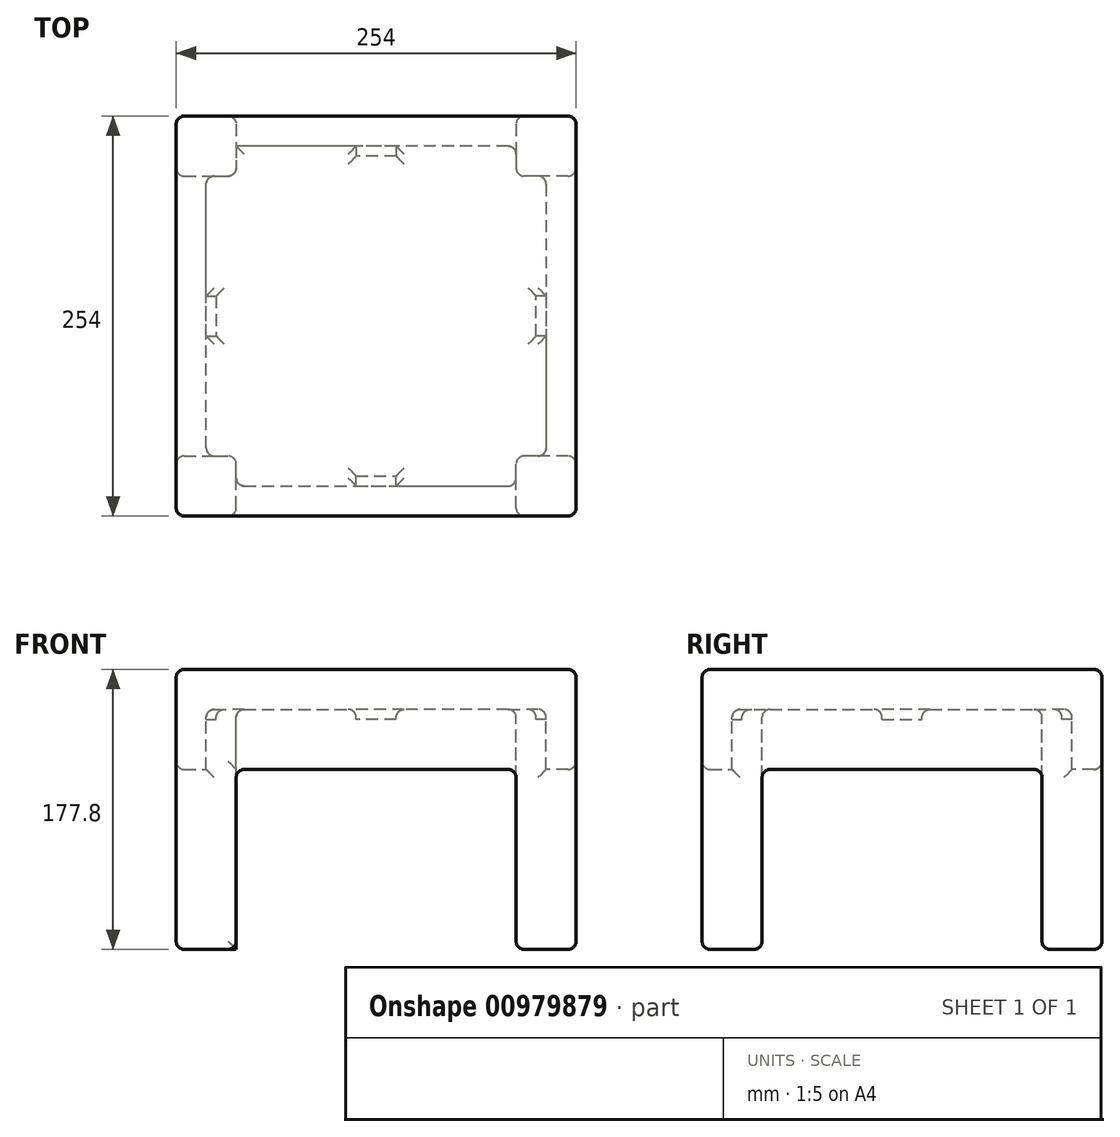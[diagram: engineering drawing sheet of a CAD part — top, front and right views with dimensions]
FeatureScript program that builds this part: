
annotation { "Feature Type Name" : "Feature", "Feature Type Description" : "" }
export const myFeature = defineFeature(function(context is Context, id is Id, definition is map)
    precondition{}
    {
        {
            var Q0;
            Q0=qCreatedBy(makeId("Top.planeOp"),FACE);
            var sketch = newSketch(context, id + "F0", { "sketchPlane" : qUnion([Q0])});
            skLineSegment(sketch, "E0", {"start": v(0, -127) * mm, "end": v(0, 127) * mm, "construction": true});
            skLineSegment(sketch, "E1", {"start": v(-127, 0) * mm, "end": v(127, 0) * mm, "construction": true});
            skLineSegment(sketch, "E2.bottom", {"start": v(-127, 127) * mm, "end": v(127, 127) * mm});
            skLineSegment(sketch, "E2.top", {"start": v(-127, -127) * mm, "end": v(127, -127) * mm});
            skLineSegment(sketch, "E2.left", {"start": v(-127, 127) * mm, "end": v(-127, -127) * mm});
            skLineSegment(sketch, "E2.right", {"start": v(127, 127) * mm, "end": v(127, -127) * mm});
            skSolve(sketch);
        }
        {
            var Q0;
            Q0 = qSketchRegion(id + "F0", true);
            extrude(context, id + "F1", {"entities" : qUnion([Q0]), "depth" : 25.4 * mm, "offsetDistance" : 25.4 * mm});
        }
        {
            var Q0;
            Q0=makeQuery(id+"F1.opExtrude","CAP_FACE",FACE,{"disambiguationData":[OSD([sQuery(id+"F0.wireOp",EDGE,"E2.bottom"),sQuery(id+"F0.wireOp",EDGE,"E2.top"),sQuery(id+"F0.wireOp",EDGE,"E2.left"),sQuery(id+"F0.wireOp",EDGE,"E2.right")])],"isStart":true});
            var sketch = newSketch(context, id + "F2", { "sketchPlane" : qUnion([Q0])});
            skLineSegment(sketch, "E3", {"start": v(0, 127) * mm, "end": v(0, -127) * mm, "construction": true});
            skLineSegment(sketch, "E4", {"start": v(-127, 0) * mm, "end": v(127, 0) * mm, "construction": true});
            skLineSegment(sketch, "E5.bottom", {"start": v(-127, 127) * mm, "end": v(-88.9, 127) * mm});
            skLineSegment(sketch, "E5.top", {"start": v(-127, 88.9) * mm, "end": v(-88.9, 88.9) * mm});
            skLineSegment(sketch, "E5.left", {"start": v(-127, 127) * mm, "end": v(-127, 88.9) * mm});
            skLineSegment(sketch, "E5.right", {"start": v(-88.9, 127) * mm, "end": v(-88.9, 88.9) * mm});
            skLineSegment(sketch, "E6.bottom", {"start": v(127, 127) * mm, "end": v(88.9, 127) * mm});
            skLineSegment(sketch, "E6.top", {"start": v(127, 88.9) * mm, "end": v(88.9, 88.9) * mm});
            skLineSegment(sketch, "E6.left", {"start": v(127, 127) * mm, "end": v(127, 88.9) * mm});
            skLineSegment(sketch, "E6.right", {"start": v(88.9, 127) * mm, "end": v(88.9, 88.9) * mm});
            skLineSegment(sketch, "E7.bottom", {"start": v(127, -127) * mm, "end": v(88.9, -127) * mm});
            skLineSegment(sketch, "E7.top", {"start": v(127, -88.9) * mm, "end": v(88.9, -88.9) * mm});
            skLineSegment(sketch, "E7.left", {"start": v(127, -127) * mm, "end": v(127, -88.9) * mm});
            skLineSegment(sketch, "E7.right", {"start": v(88.9, -127) * mm, "end": v(88.9, -88.9) * mm});
            skLineSegment(sketch, "E8.bottom", {"start": v(-127, -127) * mm, "end": v(-88.9, -127) * mm});
            skLineSegment(sketch, "E8.top", {"start": v(-127, -88.9) * mm, "end": v(-88.9, -88.9) * mm});
            skLineSegment(sketch, "E8.left", {"start": v(-127, -127) * mm, "end": v(-127, -88.9) * mm});
            skLineSegment(sketch, "E8.right", {"start": v(-88.9, -127) * mm, "end": v(-88.9, -88.9) * mm});
            skSolve(sketch);
        }
        {
            var Q0;
            Q0 = qSketchRegion(id + "F2", true);
            extrude(context, id + "F3", {"entities" : qUnion([Q0]), "operationType" : NewBodyOperationType.ADD, "depth" : 152.4 * mm, "offsetDistance" : 25.4 * mm});
        }
        {
            var Q0;
            Q0=makeQuery(id+"F1.opExtrude","CAP_FACE",FACE,{"disambiguationData":[OSD([sQuery(id+"F0.wireOp",EDGE,"E2.bottom"),sQuery(id+"F0.wireOp",EDGE,"E2.top"),sQuery(id+"F0.wireOp",EDGE,"E2.left"),sQuery(id+"F0.wireOp",EDGE,"E2.right")])],"isStart":true});
            var sketch = newSketch(context, id + "F4", { "sketchPlane" : qUnion([Q0])});
            skLineSegment(sketch, "E9", {"start": v(0, 127) * mm, "end": v(0, -127) * mm, "construction": true});
            skLineSegment(sketch, "E10", {"start": v(-127, 0) * mm, "end": v(127, 0) * mm, "construction": true});
            skLineSegment(sketch, "E11.bottom", {"start": v(-88.9, 127) * mm, "end": v(88.9, 127) * mm});
            skLineSegment(sketch, "E11.top", {"start": v(-88.9, 107.95) * mm, "end": v(88.9, 107.95) * mm});
            skLineSegment(sketch, "E11.left", {"start": v(-88.9, 127) * mm, "end": v(-88.9, 107.95) * mm});
            skLineSegment(sketch, "E11.right", {"start": v(88.9, 127) * mm, "end": v(88.9, 107.95) * mm});
            skLineSegment(sketch, "E12.bottom", {"start": v(-127, 88.9) * mm, "end": v(-107.95, 88.9) * mm});
            skLineSegment(sketch, "E12.top", {"start": v(-127, -88.9) * mm, "end": v(-107.95, -88.9) * mm});
            skLineSegment(sketch, "E12.left", {"start": v(-127, 88.9) * mm, "end": v(-127, -88.9) * mm});
            skLineSegment(sketch, "E12.right", {"start": v(-107.95, 88.9) * mm, "end": v(-107.95, -88.9) * mm});
            skLineSegment(sketch, "E13.bottom", {"start": v(127, -88.9) * mm, "end": v(107.95, -88.9) * mm});
            skLineSegment(sketch, "E13.top", {"start": v(127, 88.9) * mm, "end": v(107.95, 88.9) * mm});
            skLineSegment(sketch, "E13.left", {"start": v(127, -88.9) * mm, "end": v(127, 88.9) * mm});
            skLineSegment(sketch, "E13.right", {"start": v(107.95, -88.9) * mm, "end": v(107.95, 88.9) * mm});
            skLineSegment(sketch, "E14.bottom", {"start": v(88.9, -127) * mm, "end": v(-88.9, -127) * mm});
            skLineSegment(sketch, "E14.top", {"start": v(88.9, -107.95) * mm, "end": v(-88.9, -107.95) * mm});
            skLineSegment(sketch, "E14.left", {"start": v(88.9, -127) * mm, "end": v(88.9, -107.95) * mm});
            skLineSegment(sketch, "E14.right", {"start": v(-88.9, -127) * mm, "end": v(-88.9, -107.95) * mm});
            skSolve(sketch);
        }
        {
            var Q0;
            Q0 = qSketchRegion(id + "F4", true);
            extrude(context, id + "F5", {"entities" : qUnion([Q0]), "operationType" : NewBodyOperationType.ADD, "depth" : 38.1 * mm, "offsetDistance" : 25.4 * mm});
        }
        {
            var Q0;
            Q0=makeQuery(id+"F1.opExtrude","CAP_FACE",FACE,{"disambiguationData":[OSD([sQuery(id+"F0.wireOp",EDGE,"E2.bottom"),sQuery(id+"F0.wireOp",EDGE,"E2.top"),sQuery(id+"F0.wireOp",EDGE,"E2.left"),sQuery(id+"F0.wireOp",EDGE,"E2.right")])],"isStart":true});
            var sketch = newSketch(context, id + "F6", { "sketchPlane" : qUnion([Q0])});
            skLineSegment(sketch, "E15", {"start": v(0, 107.95) * mm, "end": v(0, -107.95) * mm, "construction": true});
            skLineSegment(sketch, "E16", {"start": v(-107.95, 0) * mm, "end": v(107.95, 0) * mm, "construction": true});
            skLineSegment(sketch, "E17.bottom", {"start": v(-107.95, -12.7) * mm, "end": v(-101.6, -12.7) * mm});
            skLineSegment(sketch, "E17.top", {"start": v(-107.95, 12.7) * mm, "end": v(-101.6, 12.7) * mm});
            skLineSegment(sketch, "E17.left", {"start": v(-107.95, -12.7) * mm, "end": v(-107.95, 12.7) * mm});
            skLineSegment(sketch, "E17.right", {"start": v(-101.6, -12.7) * mm, "end": v(-101.6, 12.7) * mm});
            skLineSegment(sketch, "E18.bottom", {"start": v(-12.7, 107.95) * mm, "end": v(12.7, 107.95) * mm});
            skLineSegment(sketch, "E18.top", {"start": v(-12.7, 101.6) * mm, "end": v(12.7, 101.6) * mm});
            skLineSegment(sketch, "E18.left", {"start": v(-12.7, 107.95) * mm, "end": v(-12.7, 101.6) * mm});
            skLineSegment(sketch, "E18.right", {"start": v(12.7, 107.95) * mm, "end": v(12.7, 101.6) * mm});
            skLineSegment(sketch, "E19.bottom", {"start": v(107.95, 12.7) * mm, "end": v(101.6, 12.7) * mm});
            skLineSegment(sketch, "E19.top", {"start": v(107.95, -12.7) * mm, "end": v(101.6, -12.7) * mm});
            skLineSegment(sketch, "E19.left", {"start": v(107.95, 12.7) * mm, "end": v(107.95, -12.7) * mm});
            skLineSegment(sketch, "E19.right", {"start": v(101.6, 12.7) * mm, "end": v(101.6, -12.7) * mm});
            skLineSegment(sketch, "E20.bottom", {"start": v(12.7, -107.95) * mm, "end": v(-12.7, -107.95) * mm});
            skLineSegment(sketch, "E20.top", {"start": v(12.7, -101.6) * mm, "end": v(-12.7, -101.6) * mm});
            skLineSegment(sketch, "E20.left", {"start": v(12.7, -107.95) * mm, "end": v(12.7, -101.6) * mm});
            skLineSegment(sketch, "E20.right", {"start": v(-12.7, -107.95) * mm, "end": v(-12.7, -101.6) * mm});
            skSolve(sketch);
        }
        {
            var Q0;
            Q0 = qSketchRegion(id + "F6", true);
            extrude(context, id + "F7", {"entities" : qUnion([Q0]), "operationType" : NewBodyOperationType.ADD, "depth" : 6.35 * mm, "offsetDistance" : 25.4 * mm});
        }
        {
            var Q0;
            Q0=makeQuery(id+"F5.boolean.opBoolean","MERGE",FACE,{"derivedFrom":[makeQuery(id+"F3.boolean.opBoolean","MERGE",FACE,{"derivedFrom":[makeQuery(id+"F1.opExtrude","SWEPT_FACE",FACE,{"disambiguationData":[OSD([sQuery(id+"F0.wireOp",EDGE,"E2.top")])]}),makeQuery(id+"F3.opExtrude","SWEPT_FACE",FACE,{"disambiguationData":[OSD([sQuery(id+"F2.wireOp",EDGE,"E5.bottom")])]}),makeQuery(id+"F3.opExtrude","SWEPT_FACE",FACE,{"disambiguationData":[OSD([sQuery(id+"F2.wireOp",EDGE,"E6.bottom")])]})]}),makeQuery(id+"F5.opExtrude","SWEPT_FACE",FACE,{"disambiguationData":[OSD([sQuery(id+"F4.wireOp",EDGE,"E11.bottom")])]})]});
            var Q1;
            Q1=makeQuery(id+"F5.boolean.opBoolean","MERGE",FACE,{"derivedFrom":[makeQuery(id+"F3.boolean.opBoolean","MERGE",FACE,{"derivedFrom":[makeQuery(id+"F1.opExtrude","SWEPT_FACE",FACE,{"disambiguationData":[OSD([sQuery(id+"F0.wireOp",EDGE,"E2.right")])]}),makeQuery(id+"F3.opExtrude","SWEPT_FACE",FACE,{"disambiguationData":[OSD([sQuery(id+"F2.wireOp",EDGE,"E6.left")])]}),makeQuery(id+"F3.opExtrude","SWEPT_FACE",FACE,{"disambiguationData":[OSD([sQuery(id+"F2.wireOp",EDGE,"E7.left")])]})]}),makeQuery(id+"F5.opExtrude","SWEPT_FACE",FACE,{"disambiguationData":[OSD([sQuery(id+"F4.wireOp",EDGE,"E13.left")])]})]});
            var Q2;
            Q2=makeQuery(id+"F5.boolean.opBoolean","MERGE",FACE,{"derivedFrom":[makeQuery(id+"F3.boolean.opBoolean","MERGE",FACE,{"derivedFrom":[makeQuery(id+"F1.opExtrude","SWEPT_FACE",FACE,{"disambiguationData":[OSD([sQuery(id+"F0.wireOp",EDGE,"E2.bottom")])]}),makeQuery(id+"F3.opExtrude","SWEPT_FACE",FACE,{"disambiguationData":[OSD([sQuery(id+"F2.wireOp",EDGE,"E7.bottom")])]}),makeQuery(id+"F3.opExtrude","SWEPT_FACE",FACE,{"disambiguationData":[OSD([sQuery(id+"F2.wireOp",EDGE,"E8.bottom")])]})]}),makeQuery(id+"F5.opExtrude","SWEPT_FACE",FACE,{"disambiguationData":[OSD([sQuery(id+"F4.wireOp",EDGE,"E14.bottom")])]})]});
            var Q3;
            Q3=makeQuery(id+"F5.boolean.opBoolean","MERGE",FACE,{"derivedFrom":[makeQuery(id+"F3.boolean.opBoolean","MERGE",FACE,{"derivedFrom":[makeQuery(id+"F1.opExtrude","SWEPT_FACE",FACE,{"disambiguationData":[OSD([sQuery(id+"F0.wireOp",EDGE,"E2.left")])]}),makeQuery(id+"F3.opExtrude","SWEPT_FACE",FACE,{"disambiguationData":[OSD([sQuery(id+"F2.wireOp",EDGE,"E5.left")])]}),makeQuery(id+"F3.opExtrude","SWEPT_FACE",FACE,{"disambiguationData":[OSD([sQuery(id+"F2.wireOp",EDGE,"E8.left")])]})]}),makeQuery(id+"F5.opExtrude","SWEPT_FACE",FACE,{"disambiguationData":[OSD([sQuery(id+"F4.wireOp",EDGE,"E12.left")])]})]});
            var Q4;
            Q4=makeQuery(id+"F3.opExtrude","SWEPT_FACE",FACE,{"disambiguationData":[OSD([sQuery(id+"F2.wireOp",EDGE,"E7.right")])]});
            var Q5;
            Q5=makeQuery(id+"F3.opExtrude","SWEPT_FACE",FACE,{"disambiguationData":[OSD([sQuery(id+"F2.wireOp",EDGE,"E5.top")])]});
            var Q6;
            Q6=makeQuery(id+"F3.opExtrude","SWEPT_FACE",FACE,{"disambiguationData":[OSD([sQuery(id+"F2.wireOp",EDGE,"E8.top")])]});
            var Q7;
            Q7=makeQuery(id+"F3.opExtrude","SWEPT_FACE",FACE,{"disambiguationData":[OSD([sQuery(id+"F2.wireOp",EDGE,"E6.right")])]});
            var Q8;
            Q8=makeQuery(id+"F3.opExtrude","SWEPT_FACE",FACE,{"disambiguationData":[OSD([sQuery(id+"F2.wireOp",EDGE,"E5.right")])]});
            var Q9;
            Q9=makeQuery(id+"F3.opExtrude","SWEPT_FACE",FACE,{"disambiguationData":[OSD([sQuery(id+"F2.wireOp",EDGE,"E7.top")])]});
            var Q10;
            Q10=makeQuery(id+"F3.opExtrude","SWEPT_FACE",FACE,{"disambiguationData":[OSD([sQuery(id+"F2.wireOp",EDGE,"E6.top")])]});
            var Q11;
            Q11=makeQuery(id+"F1.opExtrude","CAP_FACE",FACE,{"disambiguationData":[OSD([sQuery(id+"F0.wireOp",EDGE,"E2.bottom"),sQuery(id+"F0.wireOp",EDGE,"E2.top"),sQuery(id+"F0.wireOp",EDGE,"E2.left"),sQuery(id+"F0.wireOp",EDGE,"E2.right")])],"isStart":true});
            fillet(context, id + "F8", {"entities" : qUnion([Q0, Q1, Q2, Q3, Q4, Q5, Q6, Q7, Q8, Q9, Q10, Q11]), "radius" : 5.08 * mm, "tangentPropagation" : true, "allowEdgeOverflow" : false});
        }
    });
